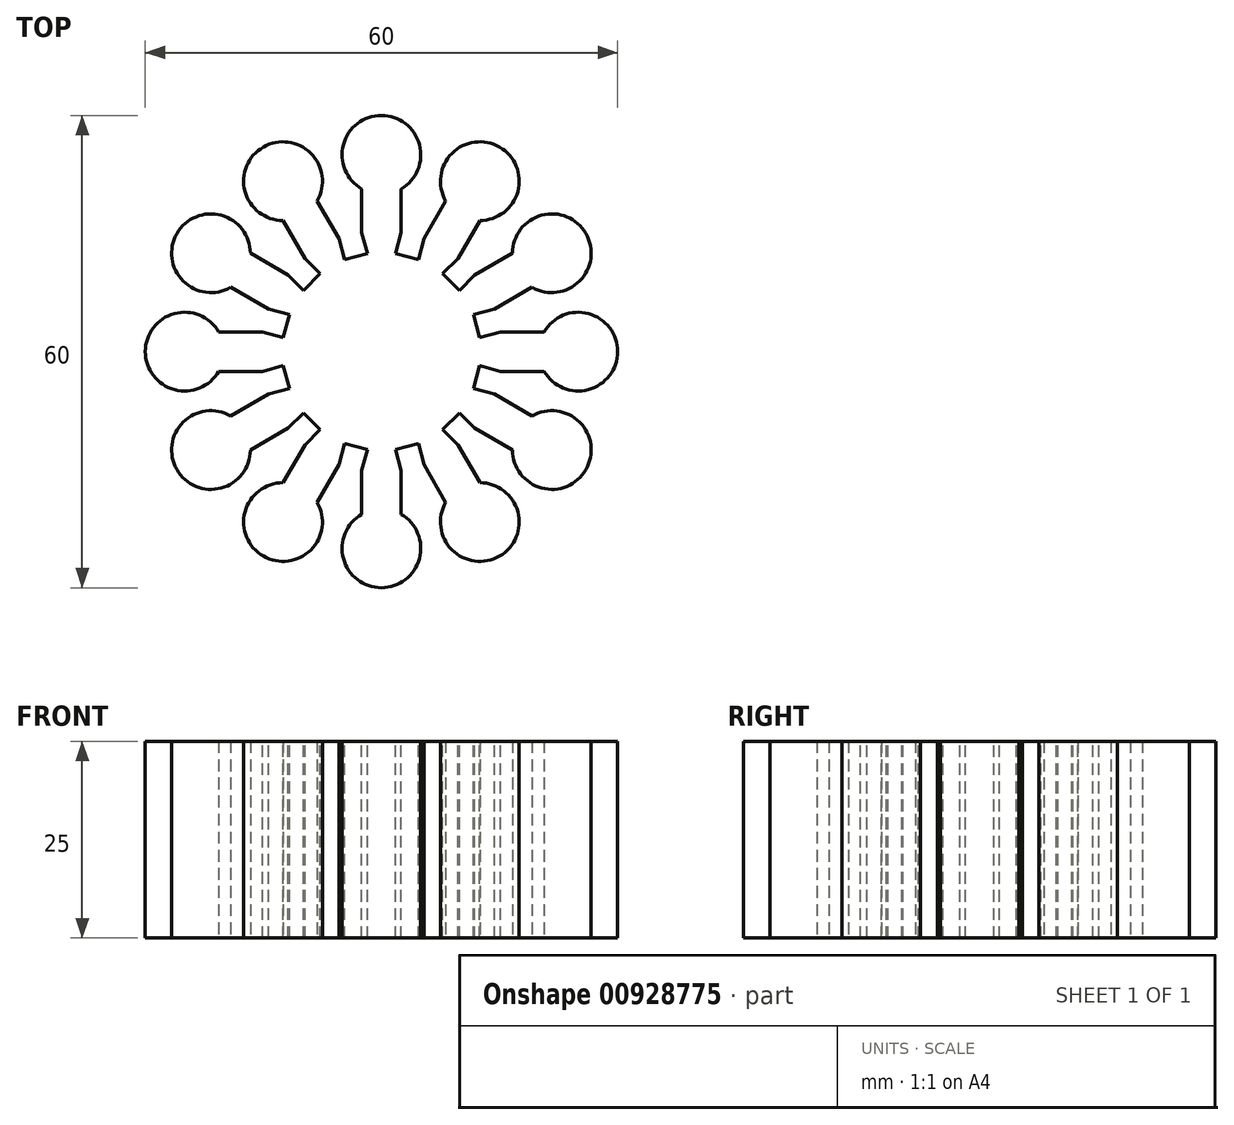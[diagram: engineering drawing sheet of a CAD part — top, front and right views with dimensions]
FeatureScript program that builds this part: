
annotation { "Feature Type Name" : "Feature", "Feature Type Description" : "" }
export const myFeature = defineFeature(function(context is Context, id is Id, definition is map)
    precondition{}
    {
        {
            var Q0;
            Q0=qCreatedBy(makeId("Top.planeOp"),FACE);
            var sketch = newSketch(context, id + "F0", { "sketchPlane" : qUnion([Q0])});
            skCircle(sketch, "E0", {"center": v(0, 0) * mm, "radius": 10 * mm});
            skSolve(sketch);
        }
        {
            var Q0;
            Q0 = qSketchRegion(id + "F0", true);
            extrude(context, id + "F1", {"entities" : qUnion([Q0]), "depth" : 25 * mm, "offsetDistance" : 25 * mm});
        }
        {
            var Q0;
            Q0=qCreatedBy(makeId("Top.planeOp"),FACE);
            var sketch = newSketch(context, id + "F2", { "sketchPlane" : qUnion([Q0])});
            skLineSegment(sketch, "E1", {"start": v(0, 0) * mm, "end": v(25, 0) * mm, "construction": true});
            skCircle(sketch, "E2", {"center": v(25, 0) * mm, "radius": 5 * mm});
            skLineSegment(sketch, "E3", {"start": v(0, 2.5) * mm, "end": v(20.67, 2.5) * mm});
            skLineSegment(sketch, "E4", {"start": v(0, -2.5) * mm, "end": v(20.67, -2.5) * mm});
            skArc(sketch, "E5", {"start": v(0, -2.5) * mm, "mid": v(-2.5, 0) * mm, "end": v(0, 2.5) * mm});
            skCircle(sketch, "E6", {"center": v(0, 0) * mm, "radius": 10 * mm});
            skSolve(sketch);
        }
        {
            var Q0;
            {var subQ0=sQuery(id+"F2.wireOp",EDGE,"E2");var subQ1=makeQuery(id+"F2.imprint","INTERSECT",VERTEX,{"derivedFrom":[subQ0,sQuery(id+"F2.wireOp",EDGE,"E3")]});Q0=makeQuery(id+"F2.imprint","IMPRINT",FACE,{"disambiguationData":[TD([[makeQuery(id+"F2.imprint","IMPRINT",EDGE,{"disambiguationData":[TD([[subQ1,-1.0]])],"derivedFrom":subQ0}),1.0]])]});}
            var Q1;
            {var subQ0=sQuery(id+"F2.wireOp",EDGE,"E3");var subQ1=sQuery(id+"F2.wireOp",EDGE,"E2");var subQ2=makeQuery(id+"F2.imprint","INTERSECT",VERTEX,{"derivedFrom":[subQ1,subQ0]});Q1=makeQuery(id+"F2.imprint","IMPRINT",FACE,{"disambiguationData":[TD([[makeQuery(id+"F2.imprint","IMPRINT",EDGE,{"disambiguationData":[TD([[subQ2,-1.0]])],"derivedFrom":subQ1}),-1.0]])]});}
            extrude(context, id + "F3", {"entities" : qUnion([Q0, Q1]), "operationType" : NewBodyOperationType.ADD, "depth" : 25 * mm, "offsetDistance" : 25 * mm});
        }
        {
            var Q0;
            Q0=qCreatedBy(makeId("Front.planeOp"),FACE);
            var sketch = newSketch(context, id + "F4", { "sketchPlane" : qUnion([Q0])});
            skLineSegment(sketch, "E7", {"start": v(0, 0) * mm, "end": v(0, 28.54) * mm, "construction": true});
            skSolve(sketch);
        }
        {
            var Q0;
            Q0=makeQuery(id+"F1.opExtrude","SWEPT_BODY",BODY,{"disambiguationData":[OSD([sQuery(id+"F0.wireOp",EDGE,"E0")])]});
            var Q1;
            Q1=sQuery(id+"F4.wireOp",EDGE,"E7");
            circularPattern(context, id + "F5", {"operationType" : NewBodyOperationType.ADD, "entities" : qUnion([Q0]), "axis" : qUnion([Q1]), "angle" : 360 * degree, "instanceCount" : 12, "equalSpace" : true});
        }
        {
            var Q0;
            {var subQ0=makeQuery(id+"F3.opExtrude","CAP_FACE",FACE,{"disambiguationData":[OSD([sQuery(id+"F2.wireOp",EDGE,"E2"),sQuery(id+"F2.wireOp",EDGE,"E3"),sQuery(id+"F2.wireOp",EDGE,"E4"),sQuery(id+"F2.wireOp",EDGE,"E6")])],"isStart":false});Q0=makeQuery(id+"FHZLJsDqTDhTd4w_2.opBoolean","MERGE",FACE,{"derivedFrom":[makeQuery(id+"F1.opExtrude","CAP_FACE",FACE,{"disambiguationData":[OSD([sQuery(id+"F0.wireOp",EDGE,"E0")])],"isStart":false}),subQ0,makeQuery(id+"F5.opPattern","COPY",FACE,{"derivedFrom":subQ0,"instanceName":"1"}),makeQuery(id+"F5.opPattern","COPY",FACE,{"derivedFrom":subQ0,"instanceName":"2"}),makeQuery(id+"F5.opPattern","COPY",FACE,{"derivedFrom":subQ0,"instanceName":"3"}),makeQuery(id+"F5.opPattern","COPY",FACE,{"derivedFrom":subQ0,"instanceName":"4"}),makeQuery(id+"F5.opPattern","COPY",FACE,{"derivedFrom":subQ0,"instanceName":"5"}),makeQuery(id+"F5.opPattern","COPY",FACE,{"derivedFrom":subQ0,"instanceName":"6"}),makeQuery(id+"F5.opPattern","COPY",FACE,{"derivedFrom":subQ0,"instanceName":"7"}),makeQuery(id+"F5.opPattern","COPY",FACE,{"derivedFrom":subQ0,"instanceName":"8"}),makeQuery(id+"F5.opPattern","COPY",FACE,{"derivedFrom":subQ0,"instanceName":"9"}),makeQuery(id+"F5.opPattern","COPY",FACE,{"derivedFrom":subQ0,"instanceName":"10"}),makeQuery(id+"F5.opPattern","COPY",FACE,{"derivedFrom":subQ0,"instanceName":"11"})]});}
            var sketch = newSketch(context, id + "F6", { "sketchPlane" : qUnion([Q0])});
            skLineSegment(sketch, "E8", {"start": v(0, 0) * mm, "end": v(12.07, 3.24) * mm, "construction": true});
            skLineSegment(sketch, "E9", {"start": v(0, 0) * mm, "end": v(-0.39, 1.45) * mm});
            skLineSegment(sketch, "E10", {"start": v(-0.39, 1.45) * mm, "end": v(18.93, 6.63) * mm});
            skLineSegment(sketch, "E11", {"start": v(18.93, 6.63) * mm, "end": v(19.32, 5.18) * mm});
            skLineSegment(sketch, "E12", {"start": v(12.07, 3.24) * mm, "end": v(11.69, 4.68) * mm});
            skLineSegment(sketch, "E13.MirrorCS", {"start": v(12.07, 3.24) * mm, "end": v(12.46, 1.79) * mm});
            skLineSegment(sketch, "E14.MirrorCS", {"start": v(0.39, -1.45) * mm, "end": v(19.7, 3.73) * mm});
            skLineSegment(sketch, "E15.MirrorCS", {"start": v(19.7, 3.73) * mm, "end": v(19.32, 5.18) * mm});
            skLineSegment(sketch, "E16.MirrorCS", {"start": v(0, 0) * mm, "end": v(0.39, -1.45) * mm});
            skSolve(sketch);
        }
        {
            var Q0;
            {var subQ13=sQuery(id+"F6.wireOp",EDGE,"E11");Q0=makeQuery(id+"F6.imprint","IMPRINT",FACE,{"disambiguationData":[TD([[makeQuery(id+"F6.imprint","IMPRINT",EDGE,{"derivedFrom":subQ13}),-1.0]])]});}
            var Q1;
            {var subQ0=sQuery(id+"F6.wireOp",EDGE,"E12");var subQ1=sQuery(id+"F6.wireOp",EDGE,"E10");var subQ2=makeQuery(id+"F6.imprint","INTERSECT",VERTEX,{"derivedFrom":[subQ1,subQ0]});Q1=makeQuery(id+"F6.imprint","IMPRINT",FACE,{"disambiguationData":[TD([[makeQuery(id+"F6.imprint","IMPRINT",EDGE,{"disambiguationData":[TD([[subQ2,-1.0]])],"derivedFrom":subQ1}),-1.0]])]});}
            var Q2;
            {var subQ0=sQuery(id+"F6.wireOp",EDGE,"E14.MirrorCS");var subQ1=sQuery(id+"F6.wireOp",EDGE,"E13.MirrorCS");var subQ2=makeQuery(id+"F6.imprint","INTERSECT",VERTEX,{"derivedFrom":[subQ1,subQ0]});Q2=makeQuery(id+"F6.imprint","IMPRINT",FACE,{"disambiguationData":[TD([[makeQuery(id+"F6.imprint","IMPRINT",EDGE,{"disambiguationData":[TD([[subQ2,1.0]])],"derivedFrom":subQ1}),1.0]])]});}
            extrude(context, id + "F7", {"entities" : qUnion([Q0, Q1, Q2]), "oppositeDirection" : true, "depth" : 25 * mm, "offsetDistance" : 25 * mm});
        }
        {
            var Q0;
            Q0=makeQuery(id+"F7.opExtrude","SWEPT_BODY",BODY,{"disambiguationData":[OSD([sQuery(id+"F6.wireOp",EDGE,"E10"),sQuery(id+"F6.wireOp",EDGE,"E11"),sQuery(id+"F6.wireOp",EDGE,"E12"),sQuery(id+"F6.wireOp",EDGE,"E13.MirrorCS"),sQuery(id+"F6.wireOp",EDGE,"E14.MirrorCS"),sQuery(id+"F6.wireOp",EDGE,"E15.MirrorCS")])]});
            var Q1;
            {var subQ2=sQuery(id+"F2.wireOp",EDGE,"E3");var subQ5=sQuery(id+"F0.wireOp",EDGE,"E0");Q1=makeQuery(id+"F5.boolean.opBoolean","SPLIT",FACE,{"disambiguationData":[TD([makeQuery(id+"F5.opPattern","COPY",FACE,{"derivedFrom":makeQuery(id+"F3.opExtrude","SWEPT_FACE",FACE,{"disambiguationData":[OSD([subQ2])]}),"instanceName":"10"})])],"derivedFrom":makeQuery(id+"F1.opExtrude","SWEPT_FACE",FACE,{"disambiguationData":[OSD([subQ5])]})});}
            circularPattern(context, id + "F8", {"operationType" : NewBodyOperationType.REMOVE, "entities" : qUnion([Q0]), "axis" : qUnion([Q1]), "angle" : 360 * degree, "instanceCount" : 12, "equalSpace" : true});
        }
        {
            var Q0;
            {var subQ0=makeQuery(id+"F3.boolean.opBoolean","MERGE",FACE,{"derivedFrom":[makeQuery(id+"F1.opExtrude","CAP_FACE",FACE,{"disambiguationData":[OSD([sQuery(id+"F0.wireOp",EDGE,"E0")])],"isStart":false}),makeQuery(id+"F3.opExtrude","CAP_FACE",FACE,{"disambiguationData":[OSD([sQuery(id+"F2.wireOp",EDGE,"E2"),sQuery(id+"F2.wireOp",EDGE,"E3"),sQuery(id+"F2.wireOp",EDGE,"E4"),sQuery(id+"F2.wireOp",EDGE,"E6")])],"isStart":false})]});Q0=makeQuery(id+"F5.boolean.opBoolean","MERGE",FACE,{"derivedFrom":[subQ0,makeQuery(id+"F5.opPattern","COPY",FACE,{"derivedFrom":subQ0,"instanceName":"1"}),makeQuery(id+"F5.opPattern","COPY",FACE,{"derivedFrom":subQ0,"instanceName":"2"}),makeQuery(id+"F5.opPattern","COPY",FACE,{"derivedFrom":subQ0,"instanceName":"3"}),makeQuery(id+"F5.opPattern","COPY",FACE,{"derivedFrom":subQ0,"instanceName":"4"}),makeQuery(id+"F5.opPattern","COPY",FACE,{"derivedFrom":subQ0,"instanceName":"5"}),makeQuery(id+"F5.opPattern","COPY",FACE,{"derivedFrom":subQ0,"instanceName":"6"}),makeQuery(id+"F5.opPattern","COPY",FACE,{"derivedFrom":subQ0,"instanceName":"7"}),makeQuery(id+"F5.opPattern","COPY",FACE,{"derivedFrom":subQ0,"instanceName":"8"}),makeQuery(id+"F5.opPattern","COPY",FACE,{"derivedFrom":subQ0,"instanceName":"9"}),makeQuery(id+"F5.opPattern","COPY",FACE,{"derivedFrom":subQ0,"instanceName":"10"}),makeQuery(id+"F5.opPattern","COPY",FACE,{"derivedFrom":subQ0,"instanceName":"11"})]});}
            var sketch = newSketch(context, id + "F9", { "sketchPlane" : qUnion([Q0])});
            skLineSegment(sketch, "E17", {"start": v(0, 0) * mm, "end": v(12.07, 3.24) * mm, "construction": true});
            skLineSegment(sketch, "E18", {"start": v(0, 0) * mm, "end": v(-0.39, 1.45) * mm});
            skLineSegment(sketch, "E19", {"start": v(-0.39, 1.45) * mm, "end": v(18.93, 6.63) * mm});
            skLineSegment(sketch, "E20", {"start": v(18.93, 6.63) * mm, "end": v(19.32, 5.18) * mm});
            skLineSegment(sketch, "E21", {"start": v(12.07, 3.24) * mm, "end": v(11.69, 4.68) * mm});
            skLineSegment(sketch, "E22.MirrorCS", {"start": v(12.07, 3.24) * mm, "end": v(12.46, 1.79) * mm});
            skLineSegment(sketch, "E23.MirrorCS", {"start": v(0.39, -1.45) * mm, "end": v(19.7, 3.73) * mm});
            skLineSegment(sketch, "E24.MirrorCS", {"start": v(19.7, 3.73) * mm, "end": v(19.32, 5.18) * mm});
            skLineSegment(sketch, "E25.MirrorCS", {"start": v(0, 0) * mm, "end": v(0.39, -1.45) * mm});
            skSolve(sketch);
        }
        {
            var Q0;
            {var subQ29=sQuery(id+"F9.wireOp",EDGE,"E18");Q0=makeQuery(id+"F9.imprint","IMPRINT",FACE,{"disambiguationData":[TD([[makeQuery(id+"F9.imprint","IMPRINT",EDGE,{"derivedFrom":subQ29}),-1.0]])]});}
            var Q1;
            {var subQ22=sQuery(id+"F9.wireOp",EDGE,"E22.MirrorCS");var subQ23=sQuery(id+"F9.wireOp",EDGE,"E21");var subQ24=makeQuery(id+"F9.imprint","INTERSECT",VERTEX,{"derivedFrom":[subQ23,subQ22]});Q1=makeQuery(id+"F9.imprint","IMPRINT",FACE,{"disambiguationData":[TD([[makeQuery(id+"F9.imprint","IMPRINT",EDGE,{"disambiguationData":[TD([[subQ24,-1.0]])],"derivedFrom":subQ23}),1.0]])]});}
            extrude(context, id + "F10", {"entities" : qUnion([Q0, Q1]), "oppositeDirection" : true, "depth" : 25 * mm, "offsetDistance" : 25 * mm});
        }
        {
            var Q0;
            Q0=qCreatedBy(makeId("Front.planeOp"),FACE);
            var sketch = newSketch(context, id + "F11", { "sketchPlane" : qUnion([Q0])});
            skLineSegment(sketch, "E26", {"start": v(0, -9.62) * mm, "end": v(0, 33) * mm});
            skSolve(sketch);
        }
        {
            var Q0;
            Q0=makeQuery(id+"F10.opExtrude","SWEPT_BODY",BODY,{"disambiguationData":[OSD([sQuery(id+"F9.wireOp",EDGE,"E18"),sQuery(id+"F9.wireOp",EDGE,"E19"),sQuery(id+"F9.wireOp",EDGE,"E21"),sQuery(id+"F9.wireOp",EDGE,"E22.MirrorCS"),sQuery(id+"F9.wireOp",EDGE,"E23.MirrorCS"),sQuery(id+"F9.wireOp",EDGE,"E25.MirrorCS")])]});
            var Q1;
            Q1=sQuery(id+"F11.wireOp",EDGE,"E26");
            circularPattern(context, id + "F12", {"operationType" : NewBodyOperationType.ADD, "entities" : qUnion([Q0]), "axis" : qUnion([Q1]), "angle" : 360 * degree, "instanceCount" : 12, "equalSpace" : true});
        }
    });
